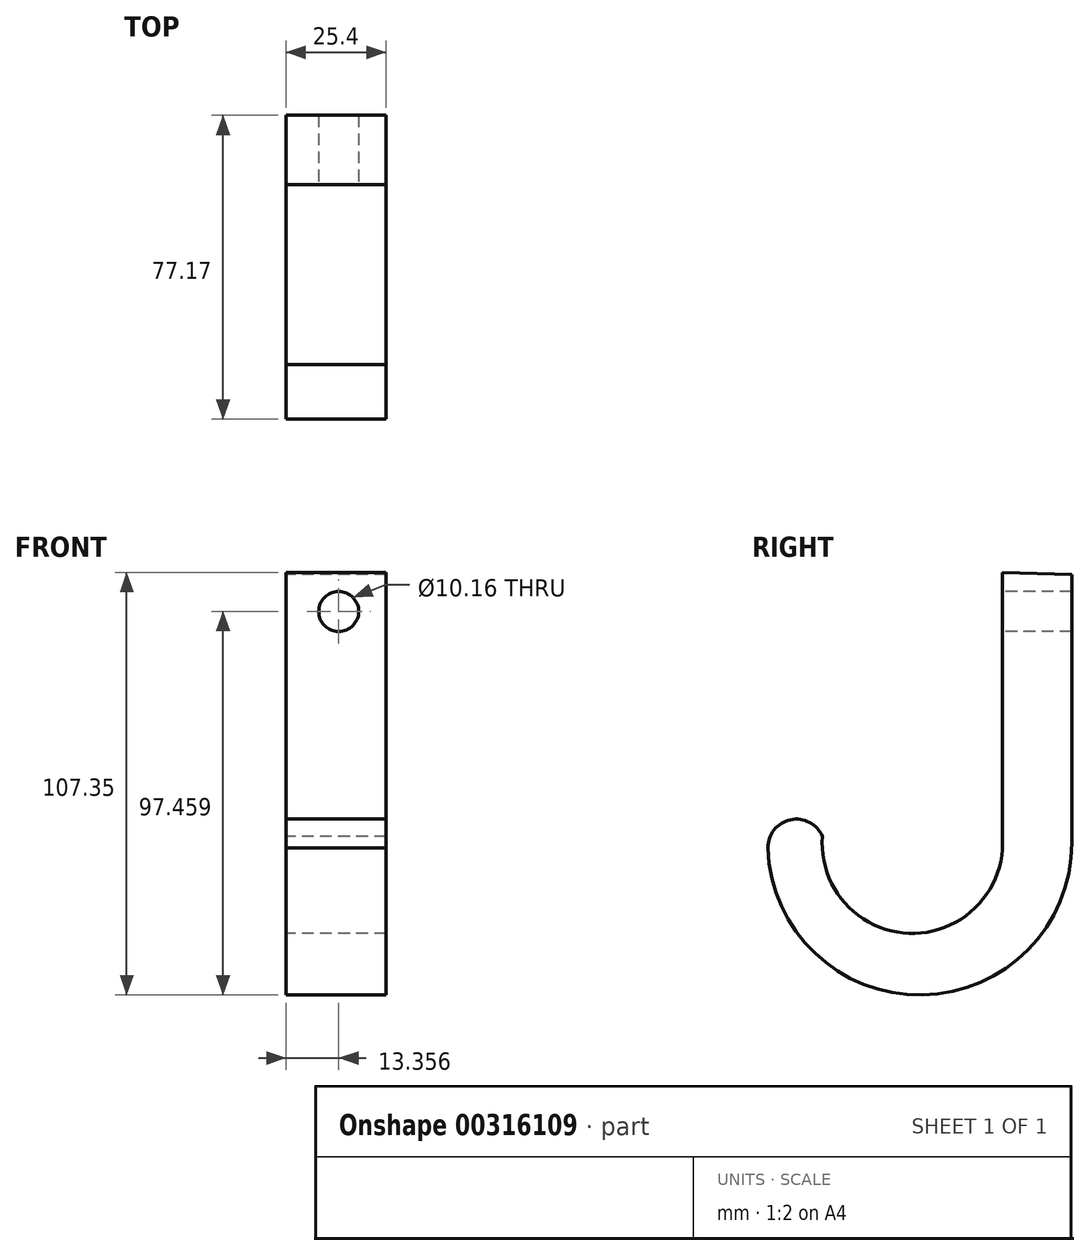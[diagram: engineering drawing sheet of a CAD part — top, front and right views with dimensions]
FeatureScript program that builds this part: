
annotation { "Feature Type Name" : "Feature", "Feature Type Description" : "" }
export const myFeature = defineFeature(function(context is Context, id is Id, definition is map)
    precondition{}
    {
        {
            var Q0;
            Q0=qCreatedBy(makeId("Right.planeOp"),FACE);
            var sketch = newSketch(context, id + "F0", { "sketchPlane" : qUnion([Q0])});
            skLineSegment(sketch, "E0", {"start": v(11.87, 47.86) * mm, "end": v(11.87, -20.4) * mm});
            skLineSegment(sketch, "E1", {"start": v(-5.69, 48.35) * mm, "end": v(-5.69, -20.4) * mm});
            skArc(sketch, "E2", {"start": v(-5.69, -20.4) * mm, "mid": v(-29.47, -43.3) * mm, "end": v(-51.44, -18.67) * mm});
            skArc(sketch, "E3", {"start": v(11.87, -20.4) * mm, "mid": v(-26.1, -59) * mm, "end": v(-65.3, -21.64) * mm});
            skArc(sketch, "E4", {"start": v(-51.44, -18.67) * mm, "mid": v(-59.59, -14.46) * mm, "end": v(-65.3, -21.64) * mm});
            skLineSegment(sketch, "E5", {"start": v(-5.69, 48.35) * mm, "end": v(11.87, 47.86) * mm});
            skSolve(sketch);
        }
        {
            var Q0;
            Q0=makeQuery(id+"F0.imprint","IMPRINT",FACE,{"disambiguationData":[TD([[makeQuery(id+"F0.imprint","IMPRINT",EDGE,{"derivedFrom":sQuery(id+"F0.wireOp",EDGE,"E0")}),-1.0]])]});
            extrude(context, id + "F1", {"entities" : qUnion([Q0]), "depth" : 25.4 * mm});
        }
        {
            var Q0;
            Q0=makeQuery(id+"F1.opExtrude","SWEPT_FACE",FACE,{"disambiguationData":[OSD([sQuery(id+"F0.wireOp",EDGE,"E1")])]});
            var sketch = newSketch(context, id + "F2", { "sketchPlane" : qUnion([Q0])});
            skCircle(sketch, "E6", {"center": v(13.36, 38.46) * mm, "radius": 3.86 * mm});
            skSolve(sketch);
        }
        {
            var Q0;
            Q0=sQuery(id+"F2.wireOp",VERTEX,"E6.center");
            var Q1;
            Q1=makeQuery(id+"F1.opExtrude","SWEPT_BODY",BODY,{"disambiguationData":[OSD([sQuery(id+"F0.wireOp",EDGE,"E0"),sQuery(id+"F0.wireOp",EDGE,"E1"),sQuery(id+"F0.wireOp",EDGE,"E2"),sQuery(id+"F0.wireOp",EDGE,"E3"),sQuery(id+"F0.wireOp",EDGE,"E4"),sQuery(id+"F0.wireOp",EDGE,"E5")])]});
            hole(context, id + "F3", {"style" : HoleStyle.SIMPLE, "endStyle" : HoleEndStyle.THROUGH, "holeDiameter" : 10.16 * mm, "tappedDepth" : 12.7 * mm, "tapClearance" : 3, "locations" : qUnion([Q0]), "scope" : qUnion([Q1])});
        }
    });
